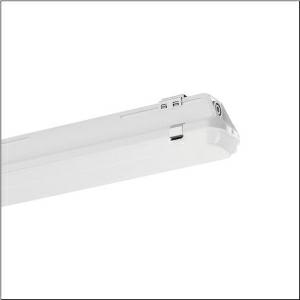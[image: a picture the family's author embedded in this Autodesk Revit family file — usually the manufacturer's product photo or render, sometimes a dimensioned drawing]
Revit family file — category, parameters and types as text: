
# Revit family: monsun_r__11_emergency_51fp207p437l3g_ce37
name_source: partatom
category: Lighting Fixtures
units: mm (PartAtom-declared; Revit-internal decimal feet)

## family parameters
Cut with Voids When Loaded = No
Host = Face
Light Source = No
Part Type = Normal
Room Calculation Point = No
Round Connector Dimension = Use Diameter
Shared = No

## types (1)
- --- (1 x LED, 890 lm, 6.4 W, 4000K)
    Apparent Load = 6 VA
    CIE Flux Codes = 45 75 93 94 100
    Color Rendering = 80
    Color Temperature = 4000K
    Default Elevation = 1800 mm
    Description = Monsun® 11 emergency, damp-proof luminaire, chain hanger, primary optical cover: enclosure, of PC, light emission: direct distribution, primary light characteristic: symmetric, installation type: suspended mounting, surface-mounted, horizontal mounting, vertical mounting, LED, rated luminous flux: 3.990lm, luminous efficacy: 164lm/W, light colour: 840, colour temperature: 4000K, control gear: ON/OFF, with terminal, 4-pole, max. 2.5mm², mains connection: 220..240V, AC, 50/60Hz, rated input power: 28W, control gear: single battery element, battery: LiFePO4, 9Ah, luminaire housing, of glass-fibre reinforced polyester, uncoated, bright grey, incl. chain hanger, length: 1.590mm, width: 90mm, height: 88mm, clip for enclosure, of stainless steel (V2A), ceiling mounting element, of stainless steel (V2A), chain hanger, of stainless steel (V2A), protection rating (complete): IP66, insulation class (complete): insulation class I (protective earthing), certification: CE, UKCA, protection symbol: D, impact resistance: IK08, permissible operating ambient temperature: +5..+35°C, standard: EN 50419, EN 60598-2-1, EN 60598-2-22, contact your sales advisor before using the luminaires in applications with unclear chemical exposure, large temperature fluctuations or condensation-forming humidity, LABS conformity tested according to VDMA 24364:2018-05, no direct snow, no direct sun, no direct rain, for indoor or canopied outdoor use, corresponds to IFS (International Featured Standards) requirements for safety and quality in the food industry, packaging unit: 1 piece
    Height = 89 mm
    Lamp = 1 x LED
    Lamp Light Flux = 890 lm
    Lamp Power = 6.4 W
    Lamp count = 1
    Length = 1590 mm
    Luminous efficacy = 139 lm/W
    Manufacturer = Siteco
    ModVariant = No
    Model = 51FP207P437L3G
    Mounting Place = Ceiling
    Mounting Type = Surface mounted
    Number of Poles = 1
    OnlyDefault = Yes
    Power Factor = 1
    Product Name = Monsun® 11 emergency
    Product group = damp-proof luminaire
    ProductGroupID = 301
    Protection Class = Protection class I
    Protection Degree = IP 66
    RLX_Detail_Level = 1
    RLX_Emergency_Light_Flux = 0 lm
    RLX_Emergency_Type = 0
    RLX_Emergency_Type_DB = No
    RlxData = <blob elided: 88969 chars, md5=6af8b051>
    Socket = socket
    Standby Power = 0 W
    System Light Flux = 890 lm
    System Power = 6 W
    Type Comments = : emergency light operation: 3 h
    Type Image = l_1349237.jpg
    URL = http://relux.com
    VarID = @adj_038357
    Voltage = 0 V
    Weight = 0.00 kg
    Width = 90 mm

## geometry (parser evidence)
native form markers: Blend x4, Sweep x14
no freeform markers — native parametric forms only
